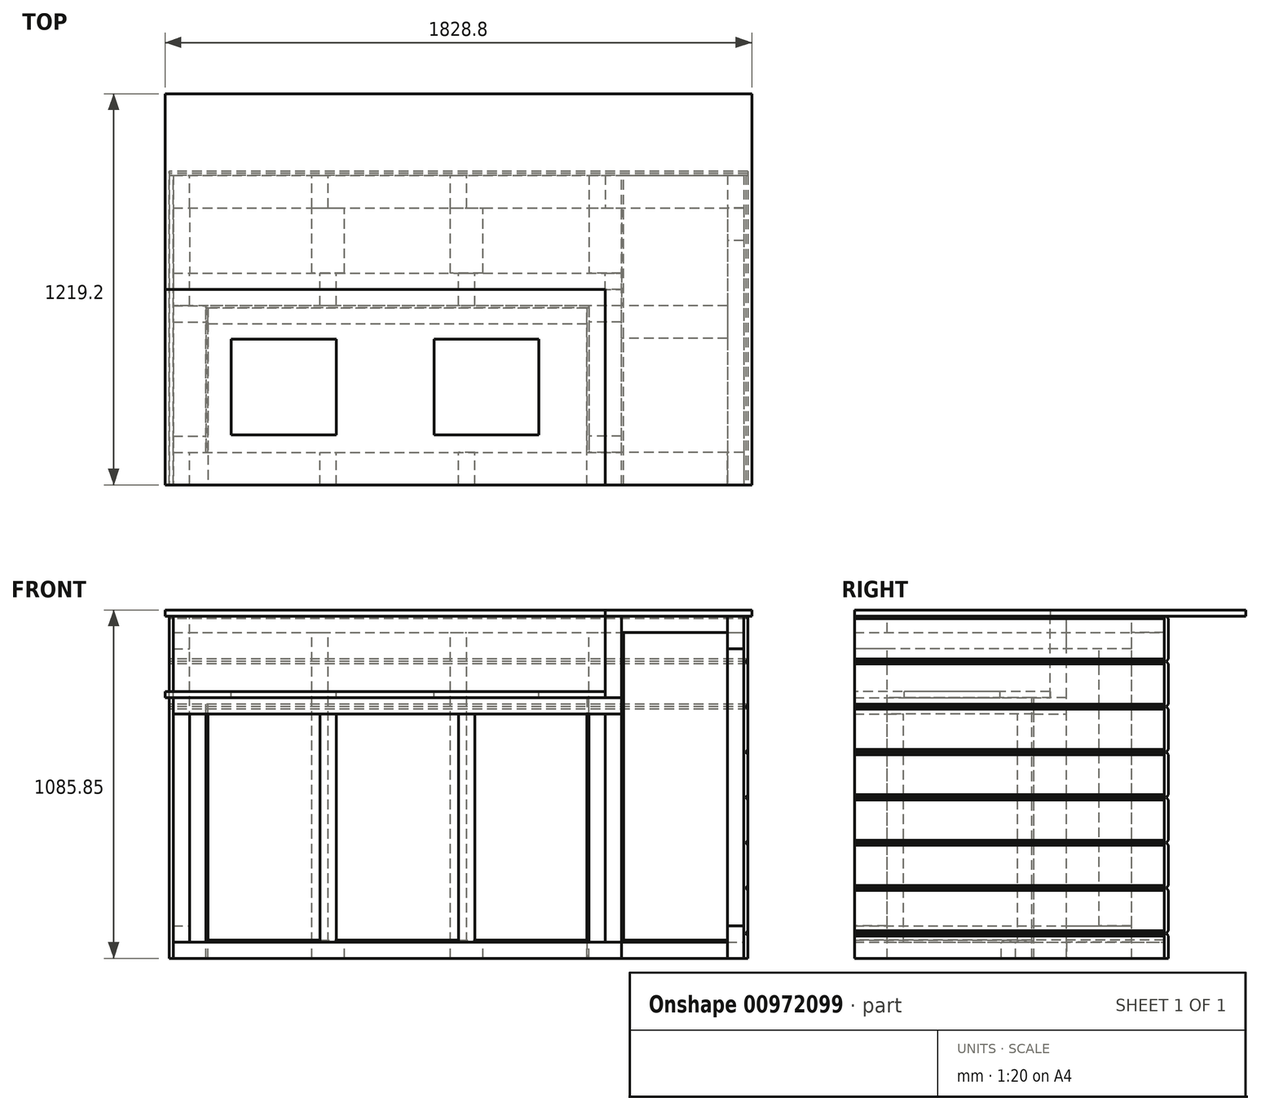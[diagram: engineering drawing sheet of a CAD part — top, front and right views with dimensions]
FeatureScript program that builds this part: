
annotation { "Feature Type Name" : "Feature", "Feature Type Description" : "" }
export const myFeature = defineFeature(function(context is Context, id is Id, definition is map)
    precondition{}
    {
        {
            var Q0;
            Q0=qCreatedBy(makeId("Top.planeOp"),FACE);
            var sketch = newSketch(context, id + "F0", { "sketchPlane" : qUnion([Q0])});
            skLineSegment(sketch, "E0", {"start": v(0, -609.6) * mm, "end": v(0, 609.6) * mm, "construction": true});
            skLineSegment(sketch, "E1", {"start": v(-914.4, 0) * mm, "end": v(914.4, 0) * mm, "construction": true});
            skLineSegment(sketch, "E2", {"start": v(-914.4, 0) * mm, "end": v(-914.4, 609.6) * mm});
            skLineSegment(sketch, "E3", {"start": v(-914.4, 609.6) * mm, "end": v(914.4, 609.6) * mm});
            skLineSegment(sketch, "E4", {"start": v(914.4, 609.6) * mm, "end": v(914.4, -609.6) * mm});
            skLineSegment(sketch, "E5", {"start": v(914.4, -609.6) * mm, "end": v(457.2, -609.6) * mm});
            skLineSegment(sketch, "E6", {"start": v(457.2, -609.6) * mm, "end": v(457.2, 0) * mm});
            skLineSegment(sketch, "E7", {"start": v(457.2, 0) * mm, "end": v(-914.4, 0) * mm});
            skSolve(sketch);
        }
        {
            var Q0;
            Q0 = qSketchRegion(id + "F0", true);
            extrude(context, id + "F1", {"entities" : qUnion([Q0]), "depth" : 19.05 * mm, "offsetDistance" : 25.4 * mm});
        }
        {
            var Q0;
            Q0=makeQuery(id+"F1.opExtrude","CAP_FACE",FACE,{"disambiguationData":[OSD([sQuery(id+"F0.wireOp",EDGE,"E2"),sQuery(id+"F0.wireOp",EDGE,"E3"),sQuery(id+"F0.wireOp",EDGE,"E4"),sQuery(id+"F0.wireOp",EDGE,"E5"),sQuery(id+"F0.wireOp",EDGE,"E6"),sQuery(id+"F0.wireOp",EDGE,"E7")])],"isStart":true});
            var sketch = newSketch(context, id + "F2", { "sketchPlane" : qUnion([Q0])});
            skLineSegment(sketch, "E8", {"start": v(-914.4, -355.6) * mm, "end": v(914.4, -355.6) * mm, "construction": true});
            skLineSegment(sketch, "E9", {"start": v(-889, -609.6) * mm, "end": v(-889, 0) * mm, "construction": true});
            skLineSegment(sketch, "E10", {"start": v(889, -609.6) * mm, "end": v(889, 609.6) * mm, "construction": true});
            skLineSegment(sketch, "E11.bottom", {"start": v(-889, -355.6) * mm, "end": v(889, -355.6) * mm});
            skLineSegment(sketch, "E11.top", {"start": v(-889, -254) * mm, "end": v(889, -254) * mm});
            skLineSegment(sketch, "E11.left", {"start": v(-889, -355.6) * mm, "end": v(-889, -254) * mm});
            skLineSegment(sketch, "E11.right", {"start": v(889, -355.6) * mm, "end": v(889, -254) * mm});
            skSolve(sketch);
        }
        {
            var Q0;
            Q0 = qSketchRegion(id + "F2", true);
            extrude(context, id + "F3", {"entities" : qUnion([Q0]), "depth" : 50.8 * mm, "offsetDistance" : 25.4 * mm});
        }
        {
            var Q0;
            Q0=makeQuery(id+"F1.opExtrude","CAP_FACE",FACE,{"disambiguationData":[OSD([sQuery(id+"F0.wireOp",EDGE,"E2"),sQuery(id+"F0.wireOp",EDGE,"E3"),sQuery(id+"F0.wireOp",EDGE,"E4"),sQuery(id+"F0.wireOp",EDGE,"E5"),sQuery(id+"F0.wireOp",EDGE,"E6"),sQuery(id+"F0.wireOp",EDGE,"E7")])],"isStart":true});
            var sketch = newSketch(context, id + "F4", { "sketchPlane" : qUnion([Q0])});
            skLineSegment(sketch, "E12.0", {"start": v(-889, -254) * mm, "end": v(889, -254) * mm, "construction": true});
            skLineSegment(sketch, "E13.bottom", {"start": v(889, -254) * mm, "end": v(838.2, -254) * mm});
            skLineSegment(sketch, "E13.top", {"start": v(889, 609.6) * mm, "end": v(838.2, 609.6) * mm});
            skLineSegment(sketch, "E13.left", {"start": v(889, -254) * mm, "end": v(889, 609.6) * mm});
            skLineSegment(sketch, "E13.right", {"start": v(838.2, -254) * mm, "end": v(838.2, 609.6) * mm});
            skLineSegment(sketch, "E14.bottom", {"start": v(-889, -254) * mm, "end": v(-838.2, -254) * mm});
            skLineSegment(sketch, "E14.top", {"start": v(-889, -50.8) * mm, "end": v(-838.2, -50.8) * mm});
            skLineSegment(sketch, "E14.left", {"start": v(-889, -254) * mm, "end": v(-889, -50.8) * mm});
            skLineSegment(sketch, "E14.right", {"start": v(-838.2, -254) * mm, "end": v(-838.2, -50.8) * mm});
            skSolve(sketch);
        }
        {
            var Q0;
            Q0 = qSketchRegion(id + "F4", true);
            extrude(context, id + "F5", {"entities" : qUnion([Q0]), "depth" : 101.6 * mm, "offsetDistance" : 25.4 * mm});
        }
        {
            var Q0;
            Q0=makeQuery(id+"F1.opExtrude","CAP_FACE",FACE,{"disambiguationData":[OSD([sQuery(id+"F0.wireOp",EDGE,"E2"),sQuery(id+"F0.wireOp",EDGE,"E3"),sQuery(id+"F0.wireOp",EDGE,"E4"),sQuery(id+"F0.wireOp",EDGE,"E5"),sQuery(id+"F0.wireOp",EDGE,"E6"),sQuery(id+"F0.wireOp",EDGE,"E7")])],"isStart":true});
            var sketch = newSketch(context, id + "F6", { "sketchPlane" : qUnion([Q0])});
            skLineSegment(sketch, "E15.0", {"start": v(838.2, -254) * mm, "end": v(838.2, 609.6) * mm, "construction": true});
            skLineSegment(sketch, "E16.bottom", {"start": v(838.2, 609.6) * mm, "end": v(508, 609.6) * mm});
            skLineSegment(sketch, "E16.top", {"start": v(838.2, 508) * mm, "end": v(508, 508) * mm});
            skLineSegment(sketch, "E16.left", {"start": v(838.2, 609.6) * mm, "end": v(838.2, 508) * mm});
            skLineSegment(sketch, "E16.right", {"start": v(508, 609.6) * mm, "end": v(508, 508) * mm});
            skSolve(sketch);
        }
        {
            var Q0;
            Q0 = qSketchRegion(id + "F6", true);
            extrude(context, id + "F7", {"entities" : qUnion([Q0]), "depth" : 50.8 * mm, "offsetDistance" : 25.4 * mm});
        }
        {
            var Q0;
            Q0=makeQuery(id+"F1.opExtrude","CAP_FACE",FACE,{"disambiguationData":[OSD([sQuery(id+"F0.wireOp",EDGE,"E2"),sQuery(id+"F0.wireOp",EDGE,"E3"),sQuery(id+"F0.wireOp",EDGE,"E4"),sQuery(id+"F0.wireOp",EDGE,"E5"),sQuery(id+"F0.wireOp",EDGE,"E6"),sQuery(id+"F0.wireOp",EDGE,"E7")])],"isStart":true});
            var sketch = newSketch(context, id + "F8", { "sketchPlane" : qUnion([Q0])});
            skPoint(sketch, "E17.0", {"position": v(-863.6, -50.8) * mm});
            skLineSegment(sketch, "E18.0", {"start": v(-889, -50.8) * mm, "end": v(-838.2, -50.8) * mm, "construction": true});
            skLineSegment(sketch, "E19.bottom", {"start": v(-889, -50.8) * mm, "end": v(508, -50.8) * mm});
            skLineSegment(sketch, "E19.top", {"start": v(-889, 0) * mm, "end": v(508, 0) * mm});
            skLineSegment(sketch, "E19.left", {"start": v(-889, -50.8) * mm, "end": v(-889, 0) * mm});
            skLineSegment(sketch, "E19.right", {"start": v(508, -50.8) * mm, "end": v(508, 0) * mm});
            skSolve(sketch);
        }
        {
            var Q0;
            Q0 = qSketchRegion(id + "F8", true);
            extrude(context, id + "F9", {"entities" : qUnion([Q0]), "depth" : 254 * mm, "offsetDistance" : 25.4 * mm});
        }
        {
            var Q0;
            Q0=makeQuery(id+"F1.opExtrude","CAP_FACE",FACE,{"disambiguationData":[OSD([sQuery(id+"F0.wireOp",EDGE,"E2"),sQuery(id+"F0.wireOp",EDGE,"E3"),sQuery(id+"F0.wireOp",EDGE,"E4"),sQuery(id+"F0.wireOp",EDGE,"E5"),sQuery(id+"F0.wireOp",EDGE,"E6"),sQuery(id+"F0.wireOp",EDGE,"E7")])],"isStart":true});
            var sketch = newSketch(context, id + "F10", { "sketchPlane" : qUnion([Q0])});
            skLineSegment(sketch, "E20.0", {"start": v(508, 609.6) * mm, "end": v(508, 508) * mm, "construction": true});
            skLineSegment(sketch, "E21.0", {"start": v(-889, 0) * mm, "end": v(508, 0) * mm, "construction": true});
            skLineSegment(sketch, "E22.bottom", {"start": v(508, 609.6) * mm, "end": v(457.2, 609.6) * mm});
            skLineSegment(sketch, "E22.top", {"start": v(508, 0) * mm, "end": v(457.2, 0) * mm});
            skLineSegment(sketch, "E22.left", {"start": v(508, 609.6) * mm, "end": v(508, 0) * mm});
            skLineSegment(sketch, "E22.right", {"start": v(457.2, 609.6) * mm, "end": v(457.2, 0) * mm});
            skSolve(sketch);
        }
        {
            var Q0;
            Q0 = qSketchRegion(id + "F10", true);
            extrude(context, id + "F11", {"entities" : qUnion([Q0]), "depth" : 254 * mm, "offsetDistance" : 25.4 * mm});
        }
        {
            var Q0;
            Q0=makeQuery(id+"F9.opExtrude","CAP_FACE",FACE,{"disambiguationData":[OSD([sQuery(id+"F8.wireOp",EDGE,"E19.bottom"),sQuery(id+"F8.wireOp",EDGE,"E19.top"),sQuery(id+"F8.wireOp",EDGE,"E19.left"),sQuery(id+"F8.wireOp",EDGE,"E19.right")])],"isStart":false});
            var sketch = newSketch(context, id + "F12", { "sketchPlane" : qUnion([Q0])});
            skLineSegment(sketch, "E23.bottom", {"start": v(508, -50.8) * mm, "end": v(-889, -50.8) * mm});
            skLineSegment(sketch, "E23.top", {"start": v(508, 50.8) * mm, "end": v(-889, 50.8) * mm});
            skLineSegment(sketch, "E23.left", {"start": v(508, -50.8) * mm, "end": v(508, 50.8) * mm});
            skLineSegment(sketch, "E23.right", {"start": v(-889, -50.8) * mm, "end": v(-889, 50.8) * mm});
            skLineSegment(sketch, "E24.0", {"start": v(508, 609.6) * mm, "end": v(508, 0) * mm, "construction": true});
            skLineSegment(sketch, "E25.bottom", {"start": v(508, 609.6) * mm, "end": v(-889, 609.6) * mm});
            skLineSegment(sketch, "E25.top", {"start": v(508, 508) * mm, "end": v(-889, 508) * mm});
            skLineSegment(sketch, "E25.left", {"start": v(508, 609.6) * mm, "end": v(508, 508) * mm});
            skLineSegment(sketch, "E25.right", {"start": v(-889, 609.6) * mm, "end": v(-889, 508) * mm});
            skSolve(sketch);
        }
        {
            var Q0;
            Q0 = qSketchRegion(id + "F12", true);
            extrude(context, id + "F13", {"entities" : qUnion([Q0]), "depth" : 50.8 * mm, "offsetDistance" : 25.4 * mm});
        }
        {
            var Q0;
            Q0=makeQuery(id+"F11.opExtrude","CAP_FACE",FACE,{"disambiguationData":[OSD([sQuery(id+"F10.wireOp",EDGE,"E22.bottom"),sQuery(id+"F10.wireOp",EDGE,"E22.top"),sQuery(id+"F10.wireOp",EDGE,"E22.left"),sQuery(id+"F10.wireOp",EDGE,"E22.right")])],"isStart":false});
            var sketch = newSketch(context, id + "F14", { "sketchPlane" : qUnion([Q0])});
            skLineSegment(sketch, "E26.0", {"start": v(508, 508) * mm, "end": v(-889, 508) * mm, "construction": true});
            skLineSegment(sketch, "E27.0", {"start": v(508, 50.8) * mm, "end": v(-889, 50.8) * mm, "construction": true});
            skLineSegment(sketch, "E28.bottom", {"start": v(-889, 50.8) * mm, "end": v(-787.4, 50.8) * mm});
            skLineSegment(sketch, "E28.top", {"start": v(-889, 508) * mm, "end": v(-787.4, 508) * mm});
            skLineSegment(sketch, "E28.left", {"start": v(-889, 50.8) * mm, "end": v(-889, 508) * mm});
            skLineSegment(sketch, "E28.right", {"start": v(-787.4, 50.8) * mm, "end": v(-787.4, 508) * mm});
            skLineSegment(sketch, "E29.bottom", {"start": v(508, 50.8) * mm, "end": v(406.4, 50.8) * mm});
            skLineSegment(sketch, "E29.top", {"start": v(508, 508) * mm, "end": v(406.4, 508) * mm});
            skLineSegment(sketch, "E29.left", {"start": v(508, 50.8) * mm, "end": v(508, 508) * mm});
            skLineSegment(sketch, "E29.right", {"start": v(406.4, 50.8) * mm, "end": v(406.4, 508) * mm});
            skSolve(sketch);
        }
        {
            var Q0;
            Q0 = qSketchRegion(id + "F14", true);
            extrude(context, id + "F15", {"entities" : qUnion([Q0]), "depth" : 50.8 * mm, "offsetDistance" : 25.4 * mm});
        }
        {
            var Q0;
            Q0=makeQuery(id+"F13.opExtrude","CAP_FACE",FACE,{"disambiguationData":[OSD([sQuery(id+"F12.wireOp",EDGE,"E23.bottom"),sQuery(id+"F12.wireOp",EDGE,"E23.top"),sQuery(id+"F12.wireOp",EDGE,"E23.left"),sQuery(id+"F12.wireOp",EDGE,"E23.right")])],"isStart":true});
            var sketch = newSketch(context, id + "F16", { "sketchPlane" : qUnion([Q0])});
            skPoint(sketch, "E30.0", {"position": v(-914.4, 0) * mm});
            skPoint(sketch, "E31.0", {"position": v(457.2, -609.6) * mm});
            skLineSegment(sketch, "E32.bottom", {"start": v(-914.4, 0) * mm, "end": v(457.2, 0) * mm});
            skLineSegment(sketch, "E32.top", {"start": v(-914.4, -609.6) * mm, "end": v(457.2, -609.6) * mm});
            skLineSegment(sketch, "E32.left", {"start": v(-914.4, 0) * mm, "end": v(-914.4, -609.6) * mm});
            skLineSegment(sketch, "E32.right", {"start": v(457.2, 0) * mm, "end": v(457.2, -609.6) * mm});
            skSolve(sketch);
        }
        {
            var Q0;
            Q0 = qSketchRegion(id + "F16", true);
            extrude(context, id + "F17", {"entities" : qUnion([Q0]), "depth" : 19.05 * mm, "offsetDistance" : 25.4 * mm});
        }
        {
            var Q0;
            Q0=makeQuery(id+"F3.opExtrude","CAP_FACE",FACE,{"disambiguationData":[OSD([sQuery(id+"F2.wireOp",EDGE,"E11.bottom"),sQuery(id+"F2.wireOp",EDGE,"E11.top"),sQuery(id+"F2.wireOp",EDGE,"E11.left"),sQuery(id+"F2.wireOp",EDGE,"E11.right")])],"isStart":false});
            var sketch = newSketch(context, id + "F18", { "sketchPlane" : qUnion([Q0])});
            skLineSegment(sketch, "E33.bottom", {"start": v(-889, -254) * mm, "end": v(-838.2, -254) * mm});
            skLineSegment(sketch, "E33.top", {"start": v(-889, -355.6) * mm, "end": v(-838.2, -355.6) * mm});
            skLineSegment(sketch, "E33.left", {"start": v(-889, -254) * mm, "end": v(-889, -355.6) * mm});
            skLineSegment(sketch, "E33.right", {"start": v(-838.2, -254) * mm, "end": v(-838.2, -355.6) * mm});
            skLineSegment(sketch, "E34.bottom", {"start": v(889, -355.6) * mm, "end": v(838.2, -355.6) * mm});
            skLineSegment(sketch, "E34.top", {"start": v(889, -254) * mm, "end": v(838.2, -254) * mm});
            skLineSegment(sketch, "E34.left", {"start": v(889, -355.6) * mm, "end": v(889, -254) * mm});
            skLineSegment(sketch, "E34.right", {"start": v(838.2, -355.6) * mm, "end": v(838.2, -254) * mm});
            skLineSegment(sketch, "E35.bottom", {"start": v(-457.2, -254) * mm, "end": v(-406.4, -254) * mm});
            skLineSegment(sketch, "E35.top", {"start": v(-457.2, -355.6) * mm, "end": v(-406.4, -355.6) * mm});
            skLineSegment(sketch, "E35.left", {"start": v(-457.2, -254) * mm, "end": v(-457.2, -355.6) * mm});
            skLineSegment(sketch, "E35.right", {"start": v(-406.4, -254) * mm, "end": v(-406.4, -355.6) * mm});
            skLineSegment(sketch, "E36.bottom", {"start": v(457.2, -355.6) * mm, "end": v(406.4, -355.6) * mm});
            skLineSegment(sketch, "E36.top", {"start": v(457.2, -254) * mm, "end": v(406.4, -254) * mm});
            skLineSegment(sketch, "E36.left", {"start": v(457.2, -355.6) * mm, "end": v(457.2, -254) * mm});
            skLineSegment(sketch, "E36.right", {"start": v(406.4, -355.6) * mm, "end": v(406.4, -254) * mm});
            skLineSegment(sketch, "E37.bottom", {"start": v(-25.4, -254) * mm, "end": v(25.4, -254) * mm});
            skLineSegment(sketch, "E37.top", {"start": v(-25.4, -355.6) * mm, "end": v(25.4, -355.6) * mm});
            skLineSegment(sketch, "E37.left", {"start": v(-25.4, -254) * mm, "end": v(-25.4, -355.6) * mm});
            skLineSegment(sketch, "E37.right", {"start": v(25.4, -254) * mm, "end": v(25.4, -355.6) * mm});
            skSolve(sketch);
        }
        {
            var Q0;
            Q0 = qSketchRegion(id + "F18", true);
            extrude(context, id + "F19", {"entities" : qUnion([Q0]), "depth" : 965.2 * mm, "offsetDistance" : 25.4 * mm});
        }
        {
            var Q0;
            Q0=makeQuery(id+"F19.opExtrude","CAP_FACE",FACE,{"disambiguationData":[OSD([sQuery(id+"F18.wireOp",EDGE,"E34.bottom"),sQuery(id+"F18.wireOp",EDGE,"E34.top"),sQuery(id+"F18.wireOp",EDGE,"E34.left"),sQuery(id+"F18.wireOp",EDGE,"E34.right")])],"isStart":false});
            var sketch = newSketch(context, id + "F20", { "sketchPlane" : qUnion([Q0])});
            skLineSegment(sketch, "E38.0", {"start": v(-889, -355.6) * mm, "end": v(-889, -254) * mm, "construction": true});
            skLineSegment(sketch, "E39.0", {"start": v(889, -355.6) * mm, "end": v(889, -254) * mm, "construction": true});
            skLineSegment(sketch, "E40.bottom", {"start": v(-889, -254) * mm, "end": v(889, -254) * mm});
            skLineSegment(sketch, "E40.top", {"start": v(-889, -355.6) * mm, "end": v(889, -355.6) * mm});
            skLineSegment(sketch, "E40.left", {"start": v(-889, -254) * mm, "end": v(-889, -355.6) * mm});
            skLineSegment(sketch, "E40.right", {"start": v(889, -254) * mm, "end": v(889, -355.6) * mm});
            skSolve(sketch);
        }
        {
            var Q0;
            Q0 = qSketchRegion(id + "F20", true);
            extrude(context, id + "F21", {"entities" : qUnion([Q0]), "depth" : 50.8 * mm, "offsetDistance" : 25.4 * mm});
        }
        {
            var Q0;
            Q0=makeQuery(id+"F13.opExtrude","CAP_FACE",FACE,{"disambiguationData":[OSD([sQuery(id+"F12.wireOp",EDGE,"E23.bottom"),sQuery(id+"F12.wireOp",EDGE,"E23.top"),sQuery(id+"F12.wireOp",EDGE,"E23.left"),sQuery(id+"F12.wireOp",EDGE,"E23.right")])],"isStart":false});
            var sketch = newSketch(context, id + "F22", { "sketchPlane" : qUnion([Q0])});
            skLineSegment(sketch, "E41.bottom", {"start": v(-889, 50.8) * mm, "end": v(-838.2, 50.8) * mm});
            skLineSegment(sketch, "E41.top", {"start": v(-889, -50.8) * mm, "end": v(-838.2, -50.8) * mm});
            skLineSegment(sketch, "E41.left", {"start": v(-889, 50.8) * mm, "end": v(-889, -50.8) * mm});
            skLineSegment(sketch, "E41.right", {"start": v(-838.2, 50.8) * mm, "end": v(-838.2, -50.8) * mm});
            skLineSegment(sketch, "E42.bottom", {"start": v(508, 50.8) * mm, "end": v(457.2, 50.8) * mm});
            skLineSegment(sketch, "E42.top", {"start": v(508, -50.8) * mm, "end": v(457.2, -50.8) * mm});
            skLineSegment(sketch, "E42.left", {"start": v(508, 50.8) * mm, "end": v(508, -50.8) * mm});
            skLineSegment(sketch, "E42.right", {"start": v(457.2, 50.8) * mm, "end": v(457.2, -50.8) * mm});
            skLineSegment(sketch, "E43.bottom", {"start": v(-431.8, 50.8) * mm, "end": v(-381, 50.8) * mm});
            skLineSegment(sketch, "E43.top", {"start": v(-431.8, -50.8) * mm, "end": v(-381, -50.8) * mm});
            skLineSegment(sketch, "E43.left", {"start": v(-431.8, 50.8) * mm, "end": v(-431.8, -50.8) * mm});
            skLineSegment(sketch, "E43.right", {"start": v(-381, 50.8) * mm, "end": v(-381, -50.8) * mm});
            skLineSegment(sketch, "E44.bottom", {"start": v(50.8, 50.8) * mm, "end": v(0, 50.8) * mm});
            skLineSegment(sketch, "E44.top", {"start": v(50.8, -50.8) * mm, "end": v(0, -50.8) * mm});
            skLineSegment(sketch, "E44.left", {"start": v(50.8, 50.8) * mm, "end": v(50.8, -50.8) * mm});
            skLineSegment(sketch, "E44.right", {"start": v(0, 50.8) * mm, "end": v(0, -50.8) * mm});
            skLineSegment(sketch, "E45.0", {"start": v(508, 609.6) * mm, "end": v(-889, 609.6) * mm, "construction": true});
            skLineSegment(sketch, "E46.0", {"start": v(508, 508) * mm, "end": v(-889, 508) * mm, "construction": true});
            skLineSegment(sketch, "E47.0", {"start": v(508, 609.6) * mm, "end": v(508, 508) * mm, "construction": true});
            skLineSegment(sketch, "E48.0", {"start": v(-889, 609.6) * mm, "end": v(-889, 508) * mm, "construction": true});
            skLineSegment(sketch, "E49.bottom", {"start": v(-889, 609.6) * mm, "end": v(-838.2, 609.6) * mm});
            skLineSegment(sketch, "E49.top", {"start": v(-889, 508) * mm, "end": v(-838.2, 508) * mm});
            skLineSegment(sketch, "E49.left", {"start": v(-889, 609.6) * mm, "end": v(-889, 508) * mm});
            skLineSegment(sketch, "E49.right", {"start": v(-838.2, 609.6) * mm, "end": v(-838.2, 508) * mm});
            skLineSegment(sketch, "E50.bottom", {"start": v(-431.8, 609.6) * mm, "end": v(-381, 609.6) * mm});
            skLineSegment(sketch, "E50.top", {"start": v(-431.8, 508) * mm, "end": v(-381, 508) * mm});
            skLineSegment(sketch, "E50.left", {"start": v(-431.8, 609.6) * mm, "end": v(-431.8, 508) * mm});
            skLineSegment(sketch, "E50.right", {"start": v(-381, 609.6) * mm, "end": v(-381, 508) * mm});
            skLineSegment(sketch, "E51.bottom", {"start": v(50.8, 609.6) * mm, "end": v(0, 609.6) * mm});
            skLineSegment(sketch, "E51.top", {"start": v(50.8, 508) * mm, "end": v(0, 508) * mm});
            skLineSegment(sketch, "E51.left", {"start": v(50.8, 609.6) * mm, "end": v(50.8, 508) * mm});
            skLineSegment(sketch, "E51.right", {"start": v(0, 609.6) * mm, "end": v(0, 508) * mm});
            skLineSegment(sketch, "E52.bottom", {"start": v(508, 609.6) * mm, "end": v(457.2, 609.6) * mm});
            skLineSegment(sketch, "E52.top", {"start": v(508, 508) * mm, "end": v(457.2, 508) * mm});
            skLineSegment(sketch, "E52.left", {"start": v(508, 609.6) * mm, "end": v(508, 508) * mm});
            skLineSegment(sketch, "E52.right", {"start": v(457.2, 609.6) * mm, "end": v(457.2, 508) * mm});
            skSolve(sketch);
        }
        {
            var Q0;
            Q0 = qSketchRegion(id + "F22", true);
            extrude(context, id + "F23", {"entities" : qUnion([Q0]), "depth" : 711.2 * mm, "offsetDistance" : 25.4 * mm});
        }
        {
            var Q0;
            Q0=makeQuery(id+"F15.opExtrude","CAP_FACE",FACE,{"disambiguationData":[OSD([sQuery(id+"F14.wireOp",EDGE,"E29.bottom"),sQuery(id+"F14.wireOp",EDGE,"E29.top"),sQuery(id+"F14.wireOp",EDGE,"E29.left"),sQuery(id+"F14.wireOp",EDGE,"E29.right")])],"isStart":false});
            var sketch = newSketch(context, id + "F24", { "sketchPlane" : qUnion([Q0])});
            skLineSegment(sketch, "E53.0", {"start": v(-889, 50.8) * mm, "end": v(-889, 508) * mm, "construction": true});
            skLineSegment(sketch, "E54.0", {"start": v(-787.4, 50.8) * mm, "end": v(-787.4, 508) * mm, "construction": true});
            skLineSegment(sketch, "E55.0", {"start": v(508, 508) * mm, "end": v(-889, 508) * mm, "construction": true});
            skLineSegment(sketch, "E56.0", {"start": v(508, 50.8) * mm, "end": v(-889, 50.8) * mm, "construction": true});
            skLineSegment(sketch, "E57.bottom", {"start": v(-889, 508) * mm, "end": v(-787.4, 508) * mm});
            skLineSegment(sketch, "E57.top", {"start": v(-889, 457.2) * mm, "end": v(-787.4, 457.2) * mm});
            skLineSegment(sketch, "E57.left", {"start": v(-889, 508) * mm, "end": v(-889, 457.2) * mm});
            skLineSegment(sketch, "E57.right", {"start": v(-787.4, 508) * mm, "end": v(-787.4, 457.2) * mm});
            skLineSegment(sketch, "E58.bottom", {"start": v(-889, 50.8) * mm, "end": v(-787.4, 50.8) * mm});
            skLineSegment(sketch, "E58.top", {"start": v(-889, 101.6) * mm, "end": v(-787.4, 101.6) * mm});
            skLineSegment(sketch, "E58.left", {"start": v(-889, 50.8) * mm, "end": v(-889, 101.6) * mm});
            skLineSegment(sketch, "E58.right", {"start": v(-787.4, 50.8) * mm, "end": v(-787.4, 101.6) * mm});
            skLineSegment(sketch, "E59.bottom", {"start": v(508, 50.8) * mm, "end": v(406.4, 50.8) * mm});
            skLineSegment(sketch, "E59.top", {"start": v(508, 101.6) * mm, "end": v(406.4, 101.6) * mm});
            skLineSegment(sketch, "E59.left", {"start": v(508, 50.8) * mm, "end": v(508, 101.6) * mm});
            skLineSegment(sketch, "E59.right", {"start": v(406.4, 50.8) * mm, "end": v(406.4, 101.6) * mm});
            skLineSegment(sketch, "E60.bottom", {"start": v(508, 508) * mm, "end": v(406.4, 508) * mm});
            skLineSegment(sketch, "E60.top", {"start": v(508, 457.2) * mm, "end": v(406.4, 457.2) * mm});
            skLineSegment(sketch, "E60.left", {"start": v(508, 508) * mm, "end": v(508, 457.2) * mm});
            skLineSegment(sketch, "E60.right", {"start": v(406.4, 508) * mm, "end": v(406.4, 457.2) * mm});
            skSolve(sketch);
        }
        {
            var Q0;
            Q0 = qSketchRegion(id + "F24", true);
            extrude(context, id + "F25", {"entities" : qUnion([Q0]), "depth" : 711.2 * mm, "offsetDistance" : 25.4 * mm});
        }
        {
            var Q0;
            Q0=makeQuery(id+"F23.opExtrude","CAP_FACE",FACE,{"disambiguationData":[OSD([sQuery(id+"F22.wireOp",EDGE,"E42.bottom"),sQuery(id+"F22.wireOp",EDGE,"E42.top"),sQuery(id+"F22.wireOp",EDGE,"E42.left"),sQuery(id+"F22.wireOp",EDGE,"E42.right")])],"isStart":false});
            var sketch = newSketch(context, id + "F26", { "sketchPlane" : qUnion([Q0])});
            skPoint(sketch, "E61.0", {"position": v(-889, 50.8) * mm});
            skPoint(sketch, "E62.0", {"position": v(-889, -50.8) * mm});
            skPoint(sketch, "E63.0", {"position": v(508, 508) * mm});
            skPoint(sketch, "E64.0", {"position": v(508, 609.6) * mm});
            skPoint(sketch, "E65.0", {"position": v(-889, 609.6) * mm});
            skLineSegment(sketch, "E66.0", {"start": v(-889, 609.6) * mm, "end": v(-889, 508) * mm, "construction": true});
            skLineSegment(sketch, "E67.bottom", {"start": v(-889, 609.6) * mm, "end": v(508, 609.6) * mm});
            skLineSegment(sketch, "E67.top", {"start": v(-889, 508) * mm, "end": v(508, 508) * mm});
            skLineSegment(sketch, "E67.left", {"start": v(-889, 609.6) * mm, "end": v(-889, 508) * mm});
            skLineSegment(sketch, "E67.right", {"start": v(508, 609.6) * mm, "end": v(508, 508) * mm});
            skLineSegment(sketch, "E68.bottom", {"start": v(508, -50.8) * mm, "end": v(-889, -50.8) * mm});
            skLineSegment(sketch, "E68.top", {"start": v(508, 50.8) * mm, "end": v(-889, 50.8) * mm});
            skLineSegment(sketch, "E68.left", {"start": v(508, -50.8) * mm, "end": v(508, 50.8) * mm});
            skLineSegment(sketch, "E68.right", {"start": v(-889, -50.8) * mm, "end": v(-889, 50.8) * mm});
            skSolve(sketch);
        }
        {
            var Q0;
            Q0 = qSketchRegion(id + "F26", true);
            extrude(context, id + "F27", {"entities" : qUnion([Q0]), "depth" : 50.8 * mm, "offsetDistance" : 25.4 * mm});
        }
        {
            var Q0;
            Q0=makeQuery(id+"F25.opExtrude","CAP_FACE",FACE,{"disambiguationData":[OSD([sQuery(id+"F24.wireOp",EDGE,"E59.bottom"),sQuery(id+"F24.wireOp",EDGE,"E59.top"),sQuery(id+"F24.wireOp",EDGE,"E59.left"),sQuery(id+"F24.wireOp",EDGE,"E59.right")])],"isStart":false});
            var sketch = newSketch(context, id + "F28", { "sketchPlane" : qUnion([Q0])});
            skPoint(sketch, "E69.0", {"position": v(-889, 508) * mm});
            skPoint(sketch, "E70.0", {"position": v(-787.4, 50.8) * mm});
            skPoint(sketch, "E71.0", {"position": v(406.4, 508) * mm});
            skPoint(sketch, "E72.0", {"position": v(508, 50.8) * mm});
            skLineSegment(sketch, "E73.bottom", {"start": v(-889, 508) * mm, "end": v(-787.4, 508) * mm});
            skLineSegment(sketch, "E73.top", {"start": v(-889, 50.8) * mm, "end": v(-787.4, 50.8) * mm});
            skLineSegment(sketch, "E73.left", {"start": v(-889, 508) * mm, "end": v(-889, 50.8) * mm});
            skLineSegment(sketch, "E73.right", {"start": v(-787.4, 508) * mm, "end": v(-787.4, 50.8) * mm});
            skLineSegment(sketch, "E74.bottom", {"start": v(508, 50.8) * mm, "end": v(406.4, 50.8) * mm});
            skLineSegment(sketch, "E74.top", {"start": v(508, 508) * mm, "end": v(406.4, 508) * mm});
            skLineSegment(sketch, "E74.left", {"start": v(508, 50.8) * mm, "end": v(508, 508) * mm});
            skLineSegment(sketch, "E74.right", {"start": v(406.4, 50.8) * mm, "end": v(406.4, 508) * mm});
            skSolve(sketch);
        }
        {
            var Q0;
            Q0 = qSketchRegion(id + "F28", true);
            extrude(context, id + "F29", {"entities" : qUnion([Q0]), "depth" : 50.8 * mm, "offsetDistance" : 25.4 * mm});
        }
        {
            var Q0;
            Q0=makeQuery(id+"F21.opExtrude","SWEPT_FACE",FACE,{"disambiguationData":[OSD([sQuery(id+"F20.wireOp",EDGE,"E40.bottom")])]});
            var sketch = newSketch(context, id + "F30", { "sketchPlane" : qUnion([Q0])});
            skLineSegment(sketch, "E75.bottom", {"start": v(-889, -1066.8) * mm, "end": v(-838.2, -1066.8) * mm});
            skLineSegment(sketch, "E75.top", {"start": v(-889, -965.2) * mm, "end": v(-838.2, -965.2) * mm});
            skLineSegment(sketch, "E75.left", {"start": v(-889, -1066.8) * mm, "end": v(-889, -965.2) * mm});
            skLineSegment(sketch, "E75.right", {"start": v(-838.2, -1066.8) * mm, "end": v(-838.2, -965.2) * mm});
            skSolve(sketch);
        }
        {
            var Q0;
            Q0 = qSketchRegion(id + "F30", true);
            extrude(context, id + "F31", {"entities" : qUnion([Q0]), "depth" : 203.2 * mm, "offsetDistance" : 25.4 * mm});
        }
        {
            var Q0;
            Q0=makeQuery(id+"F21.opExtrude","SWEPT_FACE",FACE,{"disambiguationData":[OSD([sQuery(id+"F20.wireOp",EDGE,"E40.bottom")])]});
            var sketch = newSketch(context, id + "F32", { "sketchPlane" : qUnion([Q0])});
            skLineSegment(sketch, "E76.bottom", {"start": v(889, -1066.8) * mm, "end": v(838.2, -1066.8) * mm});
            skLineSegment(sketch, "E76.top", {"start": v(889, -965.2) * mm, "end": v(838.2, -965.2) * mm});
            skLineSegment(sketch, "E76.left", {"start": v(889, -1066.8) * mm, "end": v(889, -965.2) * mm});
            skLineSegment(sketch, "E76.right", {"start": v(838.2, -1066.8) * mm, "end": v(838.2, -965.2) * mm});
            skSolve(sketch);
        }
        {
            var Q0;
            Q0 = qSketchRegion(id + "F32", true);
            extrude(context, id + "F33", {"entities" : qUnion([Q0]), "depth" : 863.6 * mm, "offsetDistance" : 25.4 * mm});
        }
        {
            var Q0;
            Q0=makeQuery(id+"F27.opExtrude","SWEPT_FACE",FACE,{"disambiguationData":[OSD([sQuery(id+"F26.wireOp",EDGE,"E67.right")])]});
            var sketch = newSketch(context, id + "F34", { "sketchPlane" : qUnion([Q0])});
            skLineSegment(sketch, "E77.bottom", {"start": v(-609.6, -1066.8) * mm, "end": v(-508, -1066.8) * mm});
            skLineSegment(sketch, "E77.top", {"start": v(-609.6, -1016) * mm, "end": v(-508, -1016) * mm});
            skLineSegment(sketch, "E77.left", {"start": v(-609.6, -1066.8) * mm, "end": v(-609.6, -1016) * mm});
            skLineSegment(sketch, "E77.right", {"start": v(-508, -1066.8) * mm, "end": v(-508, -1016) * mm});
            skSolve(sketch);
        }
        {
            var Q0;
            Q0 = qSketchRegion(id + "F34", true);
            extrude(context, id + "F35", {"entities" : qUnion([Q0]), "depth" : 330.2 * mm, "offsetDistance" : 25.4 * mm});
        }
        {
            var Q0;
            Q0=makeQuery(id+"F5.opExtrude","CAP_FACE",FACE,{"disambiguationData":[OSD([sQuery(id+"F4.wireOp",EDGE,"E13.bottom"),sQuery(id+"F4.wireOp",EDGE,"E13.top"),sQuery(id+"F4.wireOp",EDGE,"E13.left"),sQuery(id+"F4.wireOp",EDGE,"E13.right")])],"isStart":false});
            var sketch = newSketch(context, id + "F36", { "sketchPlane" : qUnion([Q0])});
            skLineSegment(sketch, "E78.bottom", {"start": v(889, 609.6) * mm, "end": v(838.2, 609.6) * mm});
            skLineSegment(sketch, "E78.top", {"start": v(889, 508) * mm, "end": v(838.2, 508) * mm});
            skLineSegment(sketch, "E78.left", {"start": v(889, 609.6) * mm, "end": v(889, 508) * mm});
            skLineSegment(sketch, "E78.right", {"start": v(838.2, 609.6) * mm, "end": v(838.2, 508) * mm});
            skLineSegment(sketch, "E79.bottom", {"start": v(889, -254) * mm, "end": v(838.2, -254) * mm});
            skLineSegment(sketch, "E79.top", {"start": v(889, -152.4) * mm, "end": v(838.2, -152.4) * mm});
            skLineSegment(sketch, "E79.left", {"start": v(889, -254) * mm, "end": v(889, -152.4) * mm});
            skLineSegment(sketch, "E79.right", {"start": v(838.2, -254) * mm, "end": v(838.2, -152.4) * mm});
            skSolve(sketch);
        }
        {
            var Q0;
            Q0 = qSketchRegion(id + "F36", true);
            extrude(context, id + "F37", {"entities" : qUnion([Q0]), "endBound" : BoundingType.UP_TO_NEXT, "depth" : 25.4 * mm, "offsetDistance" : 25.4 * mm});
        }
        {
            var Q0;
            Q0=makeQuery(id+"F27.opExtrude","SWEPT_FACE",FACE,{"disambiguationData":[OSD([sQuery(id+"F26.wireOp",EDGE,"E68.bottom")])]});
            var sketch = newSketch(context, id + "F38", { "sketchPlane" : qUnion([Q0])});
            skLineSegment(sketch, "E80.bottom", {"start": v(-508, -1016) * mm, "end": v(-406.4, -1016) * mm});
            skLineSegment(sketch, "E80.top", {"start": v(-508, -1066.8) * mm, "end": v(-406.4, -1066.8) * mm});
            skLineSegment(sketch, "E80.left", {"start": v(-508, -1016) * mm, "end": v(-508, -1066.8) * mm});
            skLineSegment(sketch, "E80.right", {"start": v(-406.4, -1016) * mm, "end": v(-406.4, -1066.8) * mm});
            skSolve(sketch);
        }
        {
            var Q0;
            Q0 = qSketchRegion(id + "F38", true);
            extrude(context, id + "F39", {"entities" : qUnion([Q0]), "endBound" : BoundingType.UP_TO_NEXT, "depth" : 25.4 * mm, "offsetDistance" : 25.4 * mm});
        }
        {
            var Q0;
            Q0=makeQuery(id+"F29.opExtrude","SWEPT_FACE",FACE,{"disambiguationData":[OSD([sQuery(id+"F28.wireOp",EDGE,"E74.left")])]});
            var sketch = newSketch(context, id + "F40", { "sketchPlane" : qUnion([Q0])});
            skLineSegment(sketch, "E81.bottom", {"start": v(-50.8, -1016) * mm, "end": v(-152.4, -1016) * mm});
            skLineSegment(sketch, "E81.top", {"start": v(-50.8, -1066.8) * mm, "end": v(-152.4, -1066.8) * mm});
            skLineSegment(sketch, "E81.left", {"start": v(-50.8, -1016) * mm, "end": v(-50.8, -1066.8) * mm});
            skLineSegment(sketch, "E81.right", {"start": v(-152.4, -1016) * mm, "end": v(-152.4, -1066.8) * mm});
            skSolve(sketch);
        }
        {
            var Q0;
            Q0 = qSketchRegion(id + "F40", true);
            extrude(context, id + "F41", {"entities" : qUnion([Q0]), "endBound" : BoundingType.UP_TO_NEXT, "depth" : 25.4 * mm, "offsetDistance" : 25.4 * mm});
        }
        {
            var Q0;
            Q0=makeQuery(id+"F3.opExtrude","SWEPT_FACE",FACE,{"disambiguationData":[OSD([sQuery(id+"F2.wireOp",EDGE,"E11.bottom")])]});
            var sketch = newSketch(context, id + "F42", { "sketchPlane" : qUnion([Q0])});
            skPoint(sketch, "E82.0", {"position": v(889, -1066.8) * mm});
            skLineSegment(sketch, "E83.bottom", {"start": v(-901.7, 0) * mm, "end": v(901.7, 0) * mm});
            skLineSegment(sketch, "E83.top", {"start": v(-901.7, -1066.8) * mm, "end": v(901.7, -1066.8) * mm});
            skLineSegment(sketch, "E83.left", {"start": v(-901.7, 0) * mm, "end": v(-901.7, -1066.8) * mm});
            skLineSegment(sketch, "E83.right", {"start": v(901.7, 0) * mm, "end": v(901.7, -1066.8) * mm});
            skSolve(sketch);
        }
        {
            var Q0;
            Q0 = qSketchRegion(id + "F42", true);
            extrude(context, id + "F43", {"entities" : qUnion([Q0]), "depth" : 12.7 * mm, "offsetDistance" : 25.4 * mm});
        }
        {
            var Q0;
            Q0=makeQuery(id+"F9.opExtrude","SWEPT_FACE",FACE,{"disambiguationData":[OSD([sQuery(id+"F8.wireOp",EDGE,"E19.left")])]});
            var sketch = newSketch(context, id + "F44", { "sketchPlane" : qUnion([Q0])});
            skPoint(sketch, "E84.0", {"position": v(-355.6, 0) * mm});
            skPoint(sketch, "E85.0", {"position": v(-355.6, -1066.8) * mm});
            skPoint(sketch, "E86.0", {"position": v(609.6, -1066.8) * mm});
            skPoint(sketch, "E87.0", {"position": v(609.6, -254) * mm});
            skPoint(sketch, "E88.0", {"position": v(0, -254) * mm});
            skLineSegment(sketch, "E89", {"start": v(0, -254) * mm, "end": v(0, 0) * mm});
            skLineSegment(sketch, "E90", {"start": v(0, 0) * mm, "end": v(-355.6, 0) * mm});
            skLineSegment(sketch, "E91", {"start": v(-355.6, -1066.8) * mm, "end": v(-355.6, 0) * mm});
            skLineSegment(sketch, "E92", {"start": v(-355.6, 0) * mm, "end": v(0, 0) * mm});
            skLineSegment(sketch, "E93", {"start": v(0, -254) * mm, "end": v(609.6, -254) * mm});
            skLineSegment(sketch, "E94", {"start": v(609.6, -254) * mm, "end": v(609.6, -1066.8) * mm});
            skLineSegment(sketch, "E95", {"start": v(609.6, -1066.8) * mm, "end": v(-355.6, -1066.8) * mm});
            skSolve(sketch);
        }
        {
            var Q0;
            Q0 = qSketchRegion(id + "F44", true);
            extrude(context, id + "F45", {"entities" : qUnion([Q0]), "depth" : 12.7 * mm, "offsetDistance" : 25.4 * mm});
        }
        {
            var Q0;
            Q0=makeQuery(id+"F5.opExtrude","SWEPT_FACE",FACE,{"disambiguationData":[OSD([sQuery(id+"F4.wireOp",EDGE,"E13.left")])]});
            var sketch = newSketch(context, id + "F46", { "sketchPlane" : qUnion([Q0])});
            skPoint(sketch, "E96.0", {"position": v(355.6, 0) * mm});
            skPoint(sketch, "E97.0", {"position": v(355.6, -1066.8) * mm});
            skPoint(sketch, "E98.0", {"position": v(-609.6, -1066.8) * mm});
            skPoint(sketch, "E99.0", {"position": v(-609.6, 0) * mm});
            skLineSegment(sketch, "E100.bottom", {"start": v(-609.6, 0) * mm, "end": v(355.6, 0) * mm, "construction": true});
            skLineSegment(sketch, "E100.top", {"start": v(-609.6, -1066.8) * mm, "end": v(355.6, -1066.8) * mm, "construction": true});
            skLineSegment(sketch, "E100.left", {"start": v(-609.6, 0) * mm, "end": v(-609.6, -1066.8) * mm, "construction": true});
            skLineSegment(sketch, "E100.right", {"start": v(355.6, 0) * mm, "end": v(355.6, -1066.8) * mm, "construction": true});
            skLineSegment(sketch, "E101.bottom", {"start": v(-609.6, 0) * mm, "end": v(355.6, 0) * mm});
            skLineSegment(sketch, "E101.top", {"start": v(-609.6, -1066.8) * mm, "end": v(355.6, -1066.8) * mm});
            skLineSegment(sketch, "E101.left", {"start": v(-609.6, 0) * mm, "end": v(-609.6, -1066.8) * mm});
            skLineSegment(sketch, "E101.right", {"start": v(355.6, 0) * mm, "end": v(355.6, -1066.8) * mm});
            skSolve(sketch);
        }
        {
            var Q0;
            Q0 = qSketchRegion(id + "F46", true);
            extrude(context, id + "F47", {"entities" : qUnion([Q0]), "depth" : 12.7 * mm, "offsetDistance" : 25.4 * mm});
        }
        {
            var Q0;
            Q0=makeQuery(id+"F13.opExtrude","SWEPT_FACE",FACE,{"disambiguationData":[OSD([sQuery(id+"F12.wireOp",EDGE,"E23.top")])]});
            var sketch = newSketch(context, id + "F48", { "sketchPlane" : qUnion([Q0])});
            skPoint(sketch, "E102.0", {"position": v(-787.4, -254) * mm});
            skPoint(sketch, "E103.0", {"position": v(406.4, -1066.8) * mm});
            skLineSegment(sketch, "E104.bottom", {"start": v(406.4, -1066.8) * mm, "end": v(-787.4, -1066.8) * mm});
            skLineSegment(sketch, "E104.top", {"start": v(406.4, -254) * mm, "end": v(-787.4, -254) * mm});
            skLineSegment(sketch, "E104.left", {"start": v(406.4, -1066.8) * mm, "end": v(406.4, -254) * mm});
            skLineSegment(sketch, "E104.right", {"start": v(-787.4, -1066.8) * mm, "end": v(-787.4, -254) * mm});
            skSolve(sketch);
        }
        {
            var Q0;
            Q0 = qSketchRegion(id + "F48", true);
            extrude(context, id + "F49", {"entities" : qUnion([Q0]), "depth" : 6.35 * mm, "offsetDistance" : 25.4 * mm});
        }
        {
            var Q0;
            Q0=makeQuery(id+"F15.opExtrude","SWEPT_FACE",FACE,{"disambiguationData":[OSD([sQuery(id+"F14.wireOp",EDGE,"E29.right")])]});
            var sketch = newSketch(context, id + "F50", { "sketchPlane" : qUnion([Q0])});
            skPoint(sketch, "E105.0", {"position": v(57.15, -254) * mm});
            skPoint(sketch, "E106.0", {"position": v(508, -1066.8) * mm});
            skLineSegment(sketch, "E107.bottom", {"start": v(57.15, -254) * mm, "end": v(508, -254) * mm});
            skLineSegment(sketch, "E107.top", {"start": v(57.15, -1066.8) * mm, "end": v(508, -1066.8) * mm});
            skLineSegment(sketch, "E107.left", {"start": v(57.15, -254) * mm, "end": v(57.15, -1066.8) * mm});
            skLineSegment(sketch, "E107.right", {"start": v(508, -254) * mm, "end": v(508, -1066.8) * mm});
            skSolve(sketch);
        }
        {
            var Q0;
            Q0 = qSketchRegion(id + "F50", true);
            extrude(context, id + "F51", {"entities" : qUnion([Q0]), "depth" : 6.35 * mm, "offsetDistance" : 25.4 * mm});
        }
        {
            var Q0;
            Q0=makeQuery(id+"F15.opExtrude","SWEPT_FACE",FACE,{"disambiguationData":[OSD([sQuery(id+"F14.wireOp",EDGE,"E28.right")])]});
            var sketch = newSketch(context, id + "F52", { "sketchPlane" : qUnion([Q0])});
            skPoint(sketch, "E108.0", {"position": v(-57.15, -254) * mm});
            skPoint(sketch, "E109.0", {"position": v(-508, -1066.8) * mm});
            skLineSegment(sketch, "E110.bottom", {"start": v(-508, -1066.8) * mm, "end": v(-57.15, -1066.8) * mm});
            skLineSegment(sketch, "E110.top", {"start": v(-508, -254) * mm, "end": v(-57.15, -254) * mm});
            skLineSegment(sketch, "E110.left", {"start": v(-508, -1066.8) * mm, "end": v(-508, -254) * mm});
            skLineSegment(sketch, "E110.right", {"start": v(-57.15, -1066.8) * mm, "end": v(-57.15, -254) * mm});
            skSolve(sketch);
        }
        {
            var Q0;
            Q0 = qSketchRegion(id + "F52", true);
            extrude(context, id + "F53", {"entities" : qUnion([Q0]), "depth" : 6.35 * mm, "offsetDistance" : 25.4 * mm});
        }
        {
            var Q0;
            Q0=makeQuery(id+"F21.opExtrude","SWEPT_FACE",FACE,{"disambiguationData":[OSD([sQuery(id+"F20.wireOp",EDGE,"E40.bottom")])]});
            var sketch = newSketch(context, id + "F54", { "sketchPlane" : qUnion([Q0])});
            skPoint(sketch, "E111.0", {"position": v(-457.2, -1016) * mm});
            skLineSegment(sketch, "E112.bottom", {"start": v(-457.2, -1016) * mm, "end": v(-355.6, -1016) * mm});
            skLineSegment(sketch, "E112.top", {"start": v(-457.2, -1066.8) * mm, "end": v(-355.6, -1066.8) * mm});
            skLineSegment(sketch, "E112.left", {"start": v(-457.2, -1016) * mm, "end": v(-457.2, -1066.8) * mm});
            skLineSegment(sketch, "E112.right", {"start": v(-355.6, -1016) * mm, "end": v(-355.6, -1066.8) * mm});
            skSolve(sketch);
        }
        {
            var Q0;
            Q0 = qSketchRegion(id + "F54", true);
            extrude(context, id + "F55", {"entities" : qUnion([Q0]), "endBound" : BoundingType.UP_TO_NEXT, "depth" : 25.4 * mm, "offsetDistance" : 25.4 * mm});
        }
        {
            var Q0;
            Q0=makeQuery(id+"F23.opExtrude","SWEPT_FACE",FACE,{"disambiguationData":[OSD([sQuery(id+"F22.wireOp",EDGE,"E52.left")])]});
            var sketch = newSketch(context, id + "F56", { "sketchPlane" : qUnion([Q0])});
            skPoint(sketch, "E113.0", {"position": v(-609.6, -50.8) * mm});
            skPoint(sketch, "E114.0", {"position": v(355.6, -1016) * mm});
            skLineSegment(sketch, "E115.bottom", {"start": v(-609.6, -1016) * mm, "end": v(355.6, -1016) * mm});
            skLineSegment(sketch, "E115.top", {"start": v(-609.6, -50.8) * mm, "end": v(355.6, -50.8) * mm});
            skLineSegment(sketch, "E115.left", {"start": v(-609.6, -1016) * mm, "end": v(-609.6, -50.8) * mm});
            skLineSegment(sketch, "E115.right", {"start": v(355.6, -1016) * mm, "end": v(355.6, -50.8) * mm});
            skSolve(sketch);
        }
        {
            var Q0;
            Q0 = qSketchRegion(id + "F56", true);
            extrude(context, id + "F57", {"entities" : qUnion([Q0]), "depth" : 6.35 * mm, "offsetDistance" : 25.4 * mm});
        }
        {
            var Q0;
            Q0=makeQuery(id+"F35.opExtrude","SWEPT_FACE",FACE,{"disambiguationData":[OSD([sQuery(id+"F34.wireOp",EDGE,"E77.top")])]});
            var sketch = newSketch(context, id + "F58", { "sketchPlane" : qUnion([Q0])});
            skPoint(sketch, "E116.0", {"position": v(514.35, 355.6) * mm});
            skLineSegment(sketch, "E117.bottom", {"start": v(514.35, 355.6) * mm, "end": v(838.2, 355.6) * mm});
            skLineSegment(sketch, "E117.top", {"start": v(514.35, -609.6) * mm, "end": v(838.2, -609.6) * mm});
            skLineSegment(sketch, "E117.left", {"start": v(514.35, 355.6) * mm, "end": v(514.35, -609.6) * mm});
            skLineSegment(sketch, "E117.right", {"start": v(838.2, 355.6) * mm, "end": v(838.2, -609.6) * mm});
            skSolve(sketch);
        }
        {
            var Q0;
            Q0 = qSketchRegion(id + "F58", true);
            extrude(context, id + "F59", {"entities" : qUnion([Q0]), "depth" : 6.35 * mm, "offsetDistance" : 25.4 * mm});
        }
        {
            var Q0;
            Q0=makeQuery(id+"F21.opExtrude","SWEPT_FACE",FACE,{"disambiguationData":[OSD([sQuery(id+"F20.wireOp",EDGE,"E40.bottom")])]});
            var sketch = newSketch(context, id + "F60", { "sketchPlane" : qUnion([Q0])});
            skPoint(sketch, "E118.0", {"position": v(-25.4, -1016) * mm});
            skLineSegment(sketch, "E119.bottom", {"start": v(-25.4, -1016) * mm, "end": v(76.2, -1016) * mm});
            skLineSegment(sketch, "E119.top", {"start": v(-25.4, -1066.8) * mm, "end": v(76.2, -1066.8) * mm});
            skLineSegment(sketch, "E119.left", {"start": v(-25.4, -1016) * mm, "end": v(-25.4, -1066.8) * mm});
            skLineSegment(sketch, "E119.right", {"start": v(76.2, -1016) * mm, "end": v(76.2, -1066.8) * mm});
            skSolve(sketch);
        }
        {
            var Q0;
            Q0 = qSketchRegion(id + "F60", true);
            extrude(context, id + "F61", {"entities" : qUnion([Q0]), "endBound" : BoundingType.UP_TO_NEXT, "depth" : 25.4 * mm, "offsetDistance" : 25.4 * mm});
        }
        {
            var Q0;
            Q0=makeQuery(id+"F49.opExtrude","CAP_FACE",FACE,{"disambiguationData":[OSD([sQuery(id+"F48.wireOp",EDGE,"E104.bottom"),sQuery(id+"F48.wireOp",EDGE,"E104.top"),sQuery(id+"F48.wireOp",EDGE,"E104.left"),sQuery(id+"F48.wireOp",EDGE,"E104.right")])],"isStart":false});
            var sketch = newSketch(context, id + "F62", { "sketchPlane" : qUnion([Q0])});
            skPoint(sketch, "E120.0", {"position": v(-781.05, -1066.8) * mm});
            skPoint(sketch, "E121.0", {"position": v(400.05, -1066.8) * mm});
            skLineSegment(sketch, "E122.bottom", {"start": v(400.05, -1066.8) * mm, "end": v(-781.05, -1066.8) * mm});
            skLineSegment(sketch, "E122.top", {"start": v(400.05, -1016) * mm, "end": v(-781.05, -1016) * mm});
            skLineSegment(sketch, "E122.left", {"start": v(400.05, -1066.8) * mm, "end": v(400.05, -1016) * mm});
            skLineSegment(sketch, "E122.right", {"start": v(-781.05, -1066.8) * mm, "end": v(-781.05, -1016) * mm});
            skSolve(sketch);
        }
        {
            var Q0;
            Q0 = qSketchRegion(id + "F62", true);
            extrude(context, id + "F63", {"entities" : qUnion([Q0]), "depth" : 50.8 * mm, "offsetDistance" : 25.4 * mm});
        }
        {
            var Q0;
            Q0=makeQuery(id+"F27.opExtrude","CAP_FACE",FACE,{"disambiguationData":[OSD([sQuery(id+"F26.wireOp",EDGE,"E67.bottom"),sQuery(id+"F26.wireOp",EDGE,"E67.top"),sQuery(id+"F26.wireOp",EDGE,"E67.left"),sQuery(id+"F26.wireOp",EDGE,"E67.right")])],"isStart":true});
            var sketch = newSketch(context, id + "F64", { "sketchPlane" : qUnion([Q0])});
            skPoint(sketch, "E123.0", {"position": v(-781.05, -57.15) * mm});
            skPoint(sketch, "E124.0", {"position": v(400.05, -57.15) * mm});
            skPoint(sketch, "E125.0", {"position": v(-431.8, -508) * mm});
            skPoint(sketch, "E126.0", {"position": v(0, -508) * mm});
            skPoint(sketch, "E127.0", {"position": v(-381, -508) * mm});
            skPoint(sketch, "E128.0", {"position": v(50.8, -508) * mm});
            skLineSegment(sketch, "E129", {"start": v(-431.8, -508) * mm, "end": v(-381, -508) * mm});
            skLineSegment(sketch, "E130", {"start": v(0, -508) * mm, "end": v(50.8, -508) * mm});
            skLineSegment(sketch, "E131", {"start": v(50.8, -508) * mm, "end": v(50.8, -609.6) * mm});
            skLineSegment(sketch, "E132", {"start": v(50.8, -609.6) * mm, "end": v(400.05, -609.6) * mm});
            skLineSegment(sketch, "E133", {"start": v(400.05, -609.6) * mm, "end": v(400.05, -57.15) * mm});
            skLineSegment(sketch, "E134", {"start": v(-781.05, -57.15) * mm, "end": v(400.05, -57.15) * mm});
            skLineSegment(sketch, "E135", {"start": v(-781.05, -57.15) * mm, "end": v(-781.05, -609.6) * mm});
            skLineSegment(sketch, "E136", {"start": v(-781.05, -609.6) * mm, "end": v(-431.8, -609.6) * mm});
            skLineSegment(sketch, "E137", {"start": v(-431.8, -609.6) * mm, "end": v(-431.8, -508) * mm});
            skLineSegment(sketch, "E138", {"start": v(-381, -508) * mm, "end": v(-381, -609.6) * mm});
            skLineSegment(sketch, "E139", {"start": v(-381, -609.6) * mm, "end": v(0, -609.6) * mm});
            skLineSegment(sketch, "E140", {"start": v(0, -609.6) * mm, "end": v(0, -508) * mm});
            skLineSegment(sketch, "E141", {"start": v(0, -609.6) * mm, "end": v(-381, -609.6) * mm});
            skSolve(sketch);
        }
        {
            var Q0;
            Q0 = qSketchRegion(id + "F64", true);
            extrude(context, id + "F65", {"entities" : qUnion([Q0]), "depth" : 6.35 * mm, "offsetDistance" : 25.4 * mm});
        }
        {
            var Q0;
            Q0=makeQuery(id+"F43.opExtrude","SWEPT_FACE",FACE,{"disambiguationData":[OSD([sQuery(id+"F42.wireOp",EDGE,"E83.right")])]});
            var sketch = newSketch(context, id + "F66", { "sketchPlane" : qUnion([Q0])});
            skLineSegment(sketch, "E142", {"start": v(-361.95, 0) * mm, "end": v(-361.95, -1066.8) * mm, "construction": true});
            skLineSegment(sketch, "E143", {"start": v(-361.95, 0) * mm, "end": v(-368.3, -7.87) * mm});
            skLineSegment(sketch, "E144", {"start": v(-368.3, -7.87) * mm, "end": v(-368.3, 0) * mm});
            skLineSegment(sketch, "E145", {"start": v(-368.3, 0) * mm, "end": v(-361.95, 0) * mm});
            skLineSegment(sketch, "E146", {"start": v(-355.6, -141.29) * mm, "end": v(-368.3, -141.29) * mm, "construction": true});
            skLineSegment(sketch, "E147", {"start": v(-361.95, -141.29) * mm, "end": v(-368.3, -133.41) * mm});
            skLineSegment(sketch, "E148", {"start": v(-368.3, -133.41) * mm, "end": v(-368.3, -149.16) * mm});
            skLineSegment(sketch, "E149", {"start": v(-368.3, -149.16) * mm, "end": v(-361.95, -141.29) * mm});
            skLineSegment(sketch, "E150.0.1.0", {"start": v(-361.95, -282.58) * mm, "end": v(-368.3, -274.7) * mm});
            skLineSegment(sketch, "E150.0.1.1", {"start": v(-355.6, -282.58) * mm, "end": v(-368.3, -282.58) * mm, "construction": true});
            skLineSegment(sketch, "E150.0.1.2", {"start": v(-368.3, -274.7) * mm, "end": v(-368.3, -290.45) * mm});
            skLineSegment(sketch, "E150.0.1.3", {"start": v(-368.3, -290.45) * mm, "end": v(-361.95, -282.58) * mm});
            skLineSegment(sketch, "E150.0.2.0", {"start": v(-361.95, -423.86) * mm, "end": v(-368.3, -415.99) * mm});
            skLineSegment(sketch, "E150.0.2.1", {"start": v(-355.6, -423.86) * mm, "end": v(-368.3, -423.86) * mm, "construction": true});
            skLineSegment(sketch, "E150.0.2.2", {"start": v(-368.3, -415.99) * mm, "end": v(-368.3, -431.74) * mm});
            skLineSegment(sketch, "E150.0.2.3", {"start": v(-368.3, -431.74) * mm, "end": v(-361.95, -423.86) * mm});
            skLineSegment(sketch, "E150.0.3.0", {"start": v(-361.95, -565.15) * mm, "end": v(-368.3, -557.28) * mm});
            skLineSegment(sketch, "E150.0.3.1", {"start": v(-355.6, -565.15) * mm, "end": v(-368.3, -565.15) * mm, "construction": true});
            skLineSegment(sketch, "E150.0.3.2", {"start": v(-368.3, -557.28) * mm, "end": v(-368.3, -573.02) * mm});
            skLineSegment(sketch, "E150.0.3.3", {"start": v(-368.3, -573.02) * mm, "end": v(-361.95, -565.15) * mm});
            skLineSegment(sketch, "E150.0.4.0", {"start": v(-361.95, -706.44) * mm, "end": v(-368.3, -698.56) * mm});
            skLineSegment(sketch, "E150.0.4.1", {"start": v(-355.6, -706.44) * mm, "end": v(-368.3, -706.44) * mm, "construction": true});
            skLineSegment(sketch, "E150.0.4.2", {"start": v(-368.3, -698.56) * mm, "end": v(-368.3, -714.31) * mm});
            skLineSegment(sketch, "E150.0.4.3", {"start": v(-368.3, -714.31) * mm, "end": v(-361.95, -706.44) * mm});
            skLineSegment(sketch, "E150.0.5.0", {"start": v(-361.95, -847.73) * mm, "end": v(-368.3, -839.85) * mm});
            skLineSegment(sketch, "E150.0.5.1", {"start": v(-355.6, -847.73) * mm, "end": v(-368.3, -847.73) * mm, "construction": true});
            skLineSegment(sketch, "E150.0.5.2", {"start": v(-368.3, -839.85) * mm, "end": v(-368.3, -855.6) * mm});
            skLineSegment(sketch, "E150.0.5.3", {"start": v(-368.3, -855.6) * mm, "end": v(-361.95, -847.73) * mm});
            skLineSegment(sketch, "E150.0.6.0", {"start": v(-361.95, -989.01) * mm, "end": v(-368.3, -981.14) * mm});
            skLineSegment(sketch, "E150.0.6.1", {"start": v(-355.6, -989.01) * mm, "end": v(-368.3, -989.01) * mm, "construction": true});
            skLineSegment(sketch, "E150.0.6.2", {"start": v(-368.3, -981.14) * mm, "end": v(-368.3, -996.89) * mm});
            skLineSegment(sketch, "E150.0.6.3", {"start": v(-368.3, -996.89) * mm, "end": v(-361.95, -989.01) * mm});
            skLineSegment(sketch, "E150.direction1", {"start": v(-368.3, -149.16) * mm, "end": v(-361.95, -149.16) * mm, "construction": true});
            skLineSegment(sketch, "E150.direction2", {"start": v(-368.3, -149.16) * mm, "end": v(-368.3, -290.45) * mm, "construction": true});
            skSolve(sketch);
        }
        {
            var Q0;
            Q0 = qSketchRegion(id + "F66", true);
            extrude(context, id + "F67", {"entities" : qUnion([Q0]), "operationType" : NewBodyOperationType.REMOVE, "endBound" : BoundingType.UP_TO_NEXT, "oppositeDirection" : true, "depth" : 25.4 * mm, "offsetDistance" : 25.4 * mm});
        }
        {
            var Q0;
            Q0=makeQuery(id+"F47.opExtrude","SWEPT_FACE",FACE,{"disambiguationData":[OSD([sQuery(id+"F46.wireOp",EDGE,"E101.left")])]});
            var sketch = newSketch(context, id + "F68", { "sketchPlane" : qUnion([Q0])});
            skLineSegment(sketch, "E151", {"start": v(895.35, 0) * mm, "end": v(895.35, -1066.8) * mm, "construction": true});
            skLineSegment(sketch, "E152", {"start": v(895.35, 0) * mm, "end": v(901.7, -7.87) * mm});
            skLineSegment(sketch, "E153", {"start": v(901.7, -7.87) * mm, "end": v(901.7, 0) * mm});
            skLineSegment(sketch, "E154", {"start": v(901.7, 0) * mm, "end": v(895.35, 0) * mm});
            skLineSegment(sketch, "E155", {"start": v(901.7, -141.29) * mm, "end": v(889, -141.29) * mm, "construction": true});
            skLineSegment(sketch, "E156", {"start": v(895.35, -141.29) * mm, "end": v(901.7, -133.41) * mm});
            skLineSegment(sketch, "E157", {"start": v(901.7, -133.41) * mm, "end": v(901.7, -149.16) * mm});
            skLineSegment(sketch, "E158", {"start": v(901.7, -149.16) * mm, "end": v(895.35, -141.29) * mm});
            skLineSegment(sketch, "E159.0.1.0", {"start": v(901.7, -290.45) * mm, "end": v(895.35, -282.57) * mm});
            skLineSegment(sketch, "E159.0.1.1", {"start": v(895.35, -282.58) * mm, "end": v(901.7, -274.7) * mm});
            skLineSegment(sketch, "E159.0.1.2", {"start": v(901.7, -274.7) * mm, "end": v(901.7, -290.45) * mm});
            skLineSegment(sketch, "E159.0.2.0", {"start": v(901.7, -431.74) * mm, "end": v(895.35, -423.86) * mm});
            skLineSegment(sketch, "E159.0.2.1", {"start": v(895.35, -423.86) * mm, "end": v(901.7, -415.99) * mm});
            skLineSegment(sketch, "E159.0.2.2", {"start": v(901.7, -415.99) * mm, "end": v(901.7, -431.74) * mm});
            skLineSegment(sketch, "E159.0.3.0", {"start": v(901.7, -573.02) * mm, "end": v(895.35, -565.15) * mm});
            skLineSegment(sketch, "E159.0.3.1", {"start": v(895.35, -565.15) * mm, "end": v(901.7, -557.28) * mm});
            skLineSegment(sketch, "E159.0.3.2", {"start": v(901.7, -557.28) * mm, "end": v(901.7, -573.02) * mm});
            skLineSegment(sketch, "E159.0.4.0", {"start": v(901.7, -714.31) * mm, "end": v(895.35, -706.44) * mm});
            skLineSegment(sketch, "E159.0.4.1", {"start": v(895.35, -706.44) * mm, "end": v(901.7, -698.56) * mm});
            skLineSegment(sketch, "E159.0.4.2", {"start": v(901.7, -698.56) * mm, "end": v(901.7, -714.31) * mm});
            skLineSegment(sketch, "E159.0.5.0", {"start": v(901.7, -855.6) * mm, "end": v(895.35, -847.73) * mm});
            skLineSegment(sketch, "E159.0.5.1", {"start": v(895.35, -847.73) * mm, "end": v(901.7, -839.85) * mm});
            skLineSegment(sketch, "E159.0.5.2", {"start": v(901.7, -839.85) * mm, "end": v(901.7, -855.6) * mm});
            skLineSegment(sketch, "E159.0.6.0", {"start": v(901.7, -996.89) * mm, "end": v(895.35, -989.01) * mm});
            skLineSegment(sketch, "E159.0.6.1", {"start": v(895.35, -989.01) * mm, "end": v(901.7, -981.14) * mm});
            skLineSegment(sketch, "E159.0.6.2", {"start": v(901.7, -981.14) * mm, "end": v(901.7, -996.89) * mm});
            skLineSegment(sketch, "E159.direction1", {"start": v(895.35, -149.16) * mm, "end": v(901.7, -149.16) * mm, "construction": true});
            skLineSegment(sketch, "E159.direction2", {"start": v(901.7, -149.16) * mm, "end": v(901.7, -290.45) * mm, "construction": true});
            skSolve(sketch);
        }
        {
            var Q0;
            Q0 = qSketchRegion(id + "F68", true);
            extrude(context, id + "F69", {"entities" : qUnion([Q0]), "operationType" : NewBodyOperationType.REMOVE, "endBound" : BoundingType.UP_TO_NEXT, "oppositeDirection" : true, "depth" : 25.4 * mm, "offsetDistance" : 25.4 * mm});
        }
        {
            var Q0;
            Q0=makeQuery(id+"F17.opExtrude","CAP_FACE",FACE,{"disambiguationData":[OSD([sQuery(id+"F16.wireOp",EDGE,"E32.bottom"),sQuery(id+"F16.wireOp",EDGE,"E32.top"),sQuery(id+"F16.wireOp",EDGE,"E32.left"),sQuery(id+"F16.wireOp",EDGE,"E32.right")])],"isStart":false});
            var sketch = newSketch(context, id + "F70", { "sketchPlane" : qUnion([Q0])});
            skLineSegment(sketch, "E160", {"start": v(-914.4, -304.8) * mm, "end": v(457.2, -304.8) * mm, "construction": true});
            skLineSegment(sketch, "E161", {"start": v(-228.6, -609.6) * mm, "end": v(-228.6, 0) * mm, "construction": true});
            skLineSegment(sketch, "E162.bottom", {"start": v(-76.2, -155.57) * mm, "end": v(250.83, -155.57) * mm});
            skLineSegment(sketch, "E162.top", {"start": v(-76.2, -454.02) * mm, "end": v(250.83, -454.02) * mm});
            skLineSegment(sketch, "E162.left", {"start": v(-76.2, -155.57) * mm, "end": v(-76.2, -454.02) * mm});
            skLineSegment(sketch, "E162.right", {"start": v(250.83, -155.57) * mm, "end": v(250.83, -454.02) * mm});
            skLineSegment(sketch, "E163.MirrorCS", {"start": v(-381, -155.57) * mm, "end": v(-381, -454.02) * mm});
            skLineSegment(sketch, "E164.MirrorCS", {"start": v(-708.03, -155.57) * mm, "end": v(-708.03, -454.02) * mm});
            skLineSegment(sketch, "E165.MirrorCS", {"start": v(-381, -454.02) * mm, "end": v(-708.03, -454.02) * mm});
            skLineSegment(sketch, "E166.MirrorCS", {"start": v(-381, -155.57) * mm, "end": v(-708.03, -155.57) * mm});
            skSolve(sketch);
        }
        {
            var Q0;
            Q0 = qSketchRegion(id + "F70", true);
            extrude(context, id + "F71", {"entities" : qUnion([Q0]), "operationType" : NewBodyOperationType.REMOVE, "endBound" : BoundingType.UP_TO_NEXT, "oppositeDirection" : true, "depth" : 25.4 * mm, "offsetDistance" : 25.4 * mm});
        }
    });
